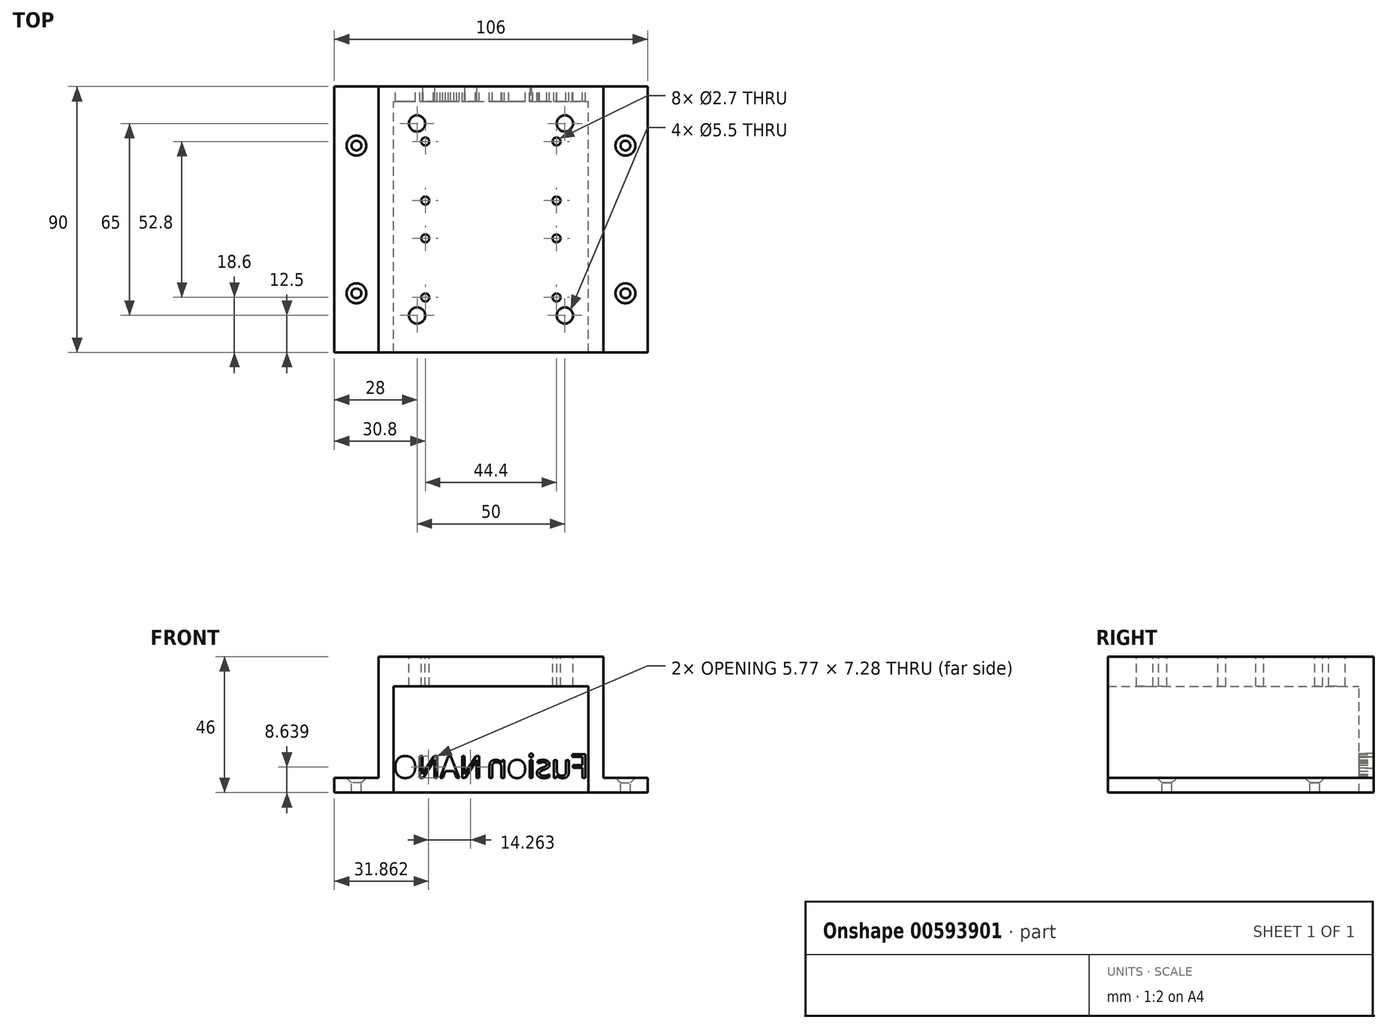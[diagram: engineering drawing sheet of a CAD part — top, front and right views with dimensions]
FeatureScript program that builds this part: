
annotation { "Feature Type Name" : "Feature", "Feature Type Description" : "" }
export const myFeature = defineFeature(function(context is Context, id is Id, definition is map)
    precondition{}
    {
        {
            var Q0;
            Q0=qCreatedBy(makeId("Front.planeOp"),FACE);
            var sketch = newSketch(context, id + "F0", { "sketchPlane" : qUnion([Q0])});
            skLineSegment(sketch, "E0", {"start": v(-53, 5) * mm, "end": v(-38, 5) * mm});
            skLineSegment(sketch, "E1", {"start": v(-38, 5) * mm, "end": v(-38, 46) * mm});
            skLineSegment(sketch, "E2", {"start": v(-38, 46) * mm, "end": v(0, 46) * mm});
            skLineSegment(sketch, "E3", {"start": v(0, 46) * mm, "end": v(0, 36) * mm});
            skLineSegment(sketch, "E4", {"start": v(0, 36) * mm, "end": v(-33, 36) * mm});
            skLineSegment(sketch, "E5", {"start": v(-33, 36) * mm, "end": v(-33, 0) * mm});
            skLineSegment(sketch, "E6", {"start": v(-33, 0) * mm, "end": v(-53, 0) * mm});
            skLineSegment(sketch, "E7", {"start": v(-53, 0) * mm, "end": v(-53, 5) * mm});
            skSolve(sketch);
        }
        {
            var Q0;
            Q0=makeQuery(id+"F0.imprint","IMPRINT",FACE,{"disambiguationData":[TD([[makeQuery(id+"F0.imprint","IMPRINT",EDGE,{"derivedFrom":sQuery(id+"F0.wireOp",EDGE,"E0")}),-1.0]])]});
            extrude(context, id + "F1", {"entities" : qUnion([Q0]), "depth" : 90 * mm, "offsetDistance" : 25 * mm});
        }
        {
            var Q0;
            Q0=makeQuery(id+"F1.opExtrude","SWEPT_FACE",FACE,{"disambiguationData":[OSD([sQuery(id+"F0.wireOp",EDGE,"E0")])]});
            var sketch = newSketch(context, id + "F2", { "sketchPlane" : qUnion([Q0])});
            skLineSegment(sketch, "E8", {"start": v(-45.5, 0) * mm, "end": v(-45.5, -90) * mm, "construction": true});
            skPoint(sketch, "E9", {"position": v(-45.5, -20) * mm});
            skPoint(sketch, "E10", {"position": v(-45.5, -70) * mm});
            skPoint(sketch, "E11", {"position": v(-45.5, -45) * mm});
            skSolve(sketch);
        }
        {
            var Q0;
            Q0=sQuery(id+"F2.wireOp",VERTEX,"E9");
            var Q1;
            Q1=sQuery(id+"F2.wireOp",VERTEX,"E10");
            var Q2;
            Q2=makeQuery(id+"F1.opExtrude","SWEPT_BODY",BODY,{"disambiguationData":[OSD([sQuery(id+"F0.wireOp",EDGE,"E0"),sQuery(id+"F0.wireOp",EDGE,"E1"),sQuery(id+"F0.wireOp",EDGE,"E2"),sQuery(id+"F0.wireOp",EDGE,"E3"),sQuery(id+"F0.wireOp",EDGE,"E4"),sQuery(id+"F0.wireOp",EDGE,"E5"),sQuery(id+"F0.wireOp",EDGE,"E6"),sQuery(id+"F0.wireOp",EDGE,"E7")])]});
            hole(context, id + "F3", {"style" : HoleStyle.C_SINK, "endStyle" : HoleEndStyle.THROUGH, "standardTappedOrClearance" : lookupTablePath({ "standard" : "ISO", "fit" : "Normal", "size" : "M3", "type" : "Clearance" }), "standardBlindInLast" : lookupTablePath({ "fit" : "Standard", "standard" : "ISO", "size" : "M3", "type" : "Clearance" }), "holeDiameter" : 3.3 * mm, "cSinkDiameter" : 6.72 * mm, "cSinkAngle" : 90 * degree, "majorDiameter" : 5 * mm, "isTappedThrough" : true, "tappedDepth" : 12 * mm, "tapClearance" : 3, "locations" : qUnion([Q0, Q1]), "scope" : qUnion([Q2])});
        }
        {
            var Q0;
            Q0=makeQuery(id+"F1.opExtrude","SWEPT_BODY",BODY,{"disambiguationData":[OSD([sQuery(id+"F0.wireOp",EDGE,"E0"),sQuery(id+"F0.wireOp",EDGE,"E1"),sQuery(id+"F0.wireOp",EDGE,"E2"),sQuery(id+"F0.wireOp",EDGE,"E3"),sQuery(id+"F0.wireOp",EDGE,"E4"),sQuery(id+"F0.wireOp",EDGE,"E5"),sQuery(id+"F0.wireOp",EDGE,"E6"),sQuery(id+"F0.wireOp",EDGE,"E7")])]});
            var Q1;
            Q1=qCreatedBy(makeId("Right.planeOp"),FACE);
            mirror(context, id + "F4", {"operationType" : NewBodyOperationType.ADD, "entities" : qUnion([Q0]), "mirrorPlane" : qUnion([Q1])});
        }
        {
            var Q0;
            {var subQ0=makeQuery(id+"F1.opExtrude","SWEPT_FACE",FACE,{"disambiguationData":[OSD([sQuery(id+"F0.wireOp",EDGE,"E4")])]});Q0=makeQuery(id+"F4.boolean.opBoolean","MERGE",FACE,{"derivedFrom":[subQ0,makeQuery(id+"F4.opPattern","COPY",FACE,{"derivedFrom":subQ0,"instanceName":"1"})]});}
            var sketch = newSketch(context, id + "F5", { "sketchPlane" : qUnion([Q0])});
            skLineSegment(sketch, "E12.bottom", {"start": v(-33, 0) * mm, "end": v(33, 0) * mm});
            skLineSegment(sketch, "E12.top", {"start": v(-33, 5) * mm, "end": v(33, 5) * mm});
            skLineSegment(sketch, "E12.left", {"start": v(-33, 0) * mm, "end": v(-33, 5) * mm});
            skLineSegment(sketch, "E12.right", {"start": v(33, 0) * mm, "end": v(33, 5) * mm});
            skSolve(sketch);
        }
        {
            var Q0;
            Q0=qSketchRegion(id+"F5",true);
            var Q1;
            Q1=makeQuery(id+"F4.opPattern","COPY",VERTEX,{"derivedFrom":makeQuery(id+"F1.opExtrude","CAP_VERTEX",VERTEX,{"disambiguationData":[OSD([sQuery(id+"F0.wireOp",EDGE,"E5"),sQuery(id+"F0.wireOp",EDGE,"E6")])],"isStart":true}),"instanceName":"1"});
            extrude(context, id + "F6", {"entities" : qUnion([Q0]), "operationType" : NewBodyOperationType.ADD, "endBound" : BoundingType.UP_TO_VERTEX, "depth" : 25 * mm, "endBoundEntityVertex" : qUnion([Q1]), "offsetDistance" : 25 * mm});
        }
        {
            var Q0;
            Q0=makeQuery(id+"F1.opExtrude","SWEPT_EDGE",EDGE,{"disambiguationData":[OSD([sQuery(id+"F0.wireOp",EDGE,"E1"),sQuery(id+"F0.wireOp",EDGE,"E2")])]});
            cPoint(context, id + "F7", {"entities" : qUnion([Q0]), "parameter" : 0.5});
        }
        {
            var Q0;
            Q0=makeQuery(id+"F4.opPattern","COPY",EDGE,{"derivedFrom":makeQuery(id+"F1.opExtrude","SWEPT_EDGE",EDGE,{"disambiguationData":[OSD([sQuery(id+"F0.wireOp",EDGE,"E1"),sQuery(id+"F0.wireOp",EDGE,"E2")])]}),"instanceName":"1"});
            cPoint(context, id + "F8", {"entities" : qUnion([Q0]), "parameter" : 0.5});
        }
        {
            var Q0;
            Q0=makeQuery(id+"F4.opPattern","COPY",EDGE,{"derivedFrom":makeQuery(id+"F1.opExtrude","SWEPT_EDGE",EDGE,{"disambiguationData":[OSD([sQuery(id+"F0.wireOp",EDGE,"E0"),sQuery(id+"F0.wireOp",EDGE,"E7")])]}),"instanceName":"1"});
            cPoint(context, id + "F9", {"entities" : qUnion([Q0]), "parameter" : 0.5});
        }
        {
            var Q0;
            Q0 = qCreatedBy(id + "F7" ,VERTEX);
            var Q1;
            Q1 = qCreatedBy(id + "F8" ,VERTEX);
            var Q2;
            Q2 = qCreatedBy(id + "F9" ,VERTEX);
            cPlane(context, id + "F10", {"entities" : qUnion([Q0, Q1, Q2]), "cplaneType" : CPlaneType.THREE_POINT, "offset" : 25 * mm, "width" : 150 * mm, "height" : 150 * mm});
        }
        {
            var Q0;
            {var subQ0=makeQuery(id+"F1.opExtrude","SWEPT_FACE",FACE,{"disambiguationData":[OSD([sQuery(id+"F0.wireOp",EDGE,"E2")])]});Q0=makeQuery(id+"F4.boolean.opBoolean","MERGE",FACE,{"derivedFrom":[subQ0,makeQuery(id+"F4.opPattern","COPY",FACE,{"derivedFrom":subQ0,"instanceName":"1"})]});}
            var sketch = newSketch(context, id + "F11", { "sketchPlane" : qUnion([Q0])});
            skPoint(sketch, "E13", {"position": v(-25, -52.5) * mm});
            skPoint(sketch, "E14.0.1.0", {"position": v(-25, -77.5) * mm});
            skLineSegment(sketch, "E14.direction1", {"start": v(-25, -52.5) * mm, "end": v(25, -52.5) * mm, "construction": true});
            skLineSegment(sketch, "E14.direction2", {"start": v(-25, -52.5) * mm, "end": v(-25, -77.5) * mm, "construction": true});
            skPoint(sketch, "E15.0.1.0", {"position": v(25, -52.5) * mm});
            skPoint(sketch, "E15.0.1.1", {"position": v(25, -77.5) * mm});
            skPoint(sketch, "E16", {"position": v(0, -52.5) * mm});
            skPoint(sketch, "E17.MirrorP", {"position": v(25, -37.5) * mm});
            skPoint(sketch, "E18.MirrorP", {"position": v(25, -12.5) * mm});
            skPoint(sketch, "E19.MirrorP", {"position": v(0, -37.5) * mm});
            skPoint(sketch, "E20.MirrorP", {"position": v(-25, -37.5) * mm});
            skPoint(sketch, "E21.MirrorP", {"position": v(-25, -12.5) * mm});
            skLineSegment(sketch, "E22.MirrorCS", {"start": v(-25, -37.5) * mm, "end": v(-25, -12.5) * mm, "construction": true});
            skLineSegment(sketch, "E23.MirrorCS", {"start": v(-25, -37.5) * mm, "end": v(25, -37.5) * mm, "construction": true});
            skSolve(sketch);
        }
        {
            var Q0;
            Q0=sQuery(id+"F11.wireOp",VERTEX,"E21.MirrorP");
            var Q1;
            Q1=sQuery(id+"F11.wireOp",VERTEX,"E18.MirrorP");
            var Q2;
            Q2=sQuery(id+"F11.wireOp",VERTEX,"E15.0.1.1");
            var Q3;
            Q3=sQuery(id+"F11.wireOp",VERTEX,"E14.0.1.0");
            var Q4;
            Q4=makeQuery(id+"F1.opExtrude","SWEPT_BODY",BODY,{"disambiguationData":[OSD([sQuery(id+"F0.wireOp",EDGE,"E0"),sQuery(id+"F0.wireOp",EDGE,"E1"),sQuery(id+"F0.wireOp",EDGE,"E2"),sQuery(id+"F0.wireOp",EDGE,"E3"),sQuery(id+"F0.wireOp",EDGE,"E4"),sQuery(id+"F0.wireOp",EDGE,"E5"),sQuery(id+"F0.wireOp",EDGE,"E6"),sQuery(id+"F0.wireOp",EDGE,"E7")])]});
            hole(context, id + "F12", {"style" : HoleStyle.SIMPLE, "endStyle" : HoleEndStyle.THROUGH, "standardTappedOrClearance" : lookupTablePath({ "standard" : "ISO", "engagement" : "50%", "pitch" : "0.75 mm", "size" : "M6", "type" : "Tapped" }), "standardBlindInLast" : lookupTablePath({ "standard" : "ISO", "engagement" : "50%", "pitch" : "0.75 mm", "size" : "M6", "type" : "Tapped" }), "holeDiameter" : 5.5 * mm, "majorDiameter" : 6 * mm, "showTappedDepth" : true, "isTappedThrough" : true, "tappedDepth" : 12 * mm, "tapClearance" : 3, "locations" : qUnion([Q0, Q1, Q2, Q3]), "scope" : qUnion([Q4])});
        }
        {
            var Q0;
            {var subQ0=makeQuery(id+"F1.opExtrude","CAP_FACE",FACE,{"disambiguationData":[OSD([sQuery(id+"F0.wireOp",EDGE,"E0"),sQuery(id+"F0.wireOp",EDGE,"E1"),sQuery(id+"F0.wireOp",EDGE,"E2"),sQuery(id+"F0.wireOp",EDGE,"E3"),sQuery(id+"F0.wireOp",EDGE,"E4"),sQuery(id+"F0.wireOp",EDGE,"E5"),sQuery(id+"F0.wireOp",EDGE,"E6"),sQuery(id+"F0.wireOp",EDGE,"E7")])],"isStart":true});Q0=makeQuery(id+"F6.boolean.opBoolean","MERGE",FACE,{"derivedFrom":[makeQuery(id+"F4.boolean.opBoolean","MERGE",FACE,{"derivedFrom":[subQ0,makeQuery(id+"F4.opPattern","COPY",FACE,{"derivedFrom":subQ0,"instanceName":"1"})]}),makeQuery(id+"F6.opExtrude","SWEPT_FACE",FACE,{"disambiguationData":[OSD([sQuery(id+"F5.wireOp",EDGE,"E12.bottom")])]})]});}
            var sketch = newSketch(context, id + "F13", { "sketchPlane" : qUnion([Q0])});
            skText(sketch, "E24", { "text": "NANO", "fontName": "NotoSans-Regular.ttf"});
            skText(sketch, "E25", { "text": "Fusion", "fontName": "NotoSans-Regular.ttf"});
            const initialGuessF13  = {"E24": [0.003, 0.005, 1, 0, 0.00734], "E25": [-0.033, 0.005, 1, 0, 0.008]};
            skSetInitialGuess(sketch, initialGuessF13);
            skSolve(sketch);
        }
        {
            var Q0;
            Q0=qSketchRegion(id+"F13",true);
            extrude(context, id + "F14", {"entities" : qUnion([Q0]), "operationType" : NewBodyOperationType.REMOVE, "oppositeDirection" : true, "depth" : 25 * mm, "offsetDistance" : 25 * mm});
        }
        {
            var Q0;
            {var subQ0=makeQuery(id+"F1.opExtrude","CAP_FACE",FACE,{"disambiguationData":[OSD([sQuery(id+"F0.wireOp",EDGE,"E0"),sQuery(id+"F0.wireOp",EDGE,"E1"),sQuery(id+"F0.wireOp",EDGE,"E2"),sQuery(id+"F0.wireOp",EDGE,"E3"),sQuery(id+"F0.wireOp",EDGE,"E4"),sQuery(id+"F0.wireOp",EDGE,"E5"),sQuery(id+"F0.wireOp",EDGE,"E6"),sQuery(id+"F0.wireOp",EDGE,"E7")])],"isStart":true});Q0=makeQuery(id+"F14.boolean.opBoolean","SPLIT",FACE,{"disambiguationData":[TD([makeQuery(id+"F14.opExtrude","SWEPT_FACE",FACE,{"disambiguationData":[OSD([sQuery(id+"F13.wireOp",EDGE,"E25.sketch_text.stroke-72")])]})])],"derivedFrom":makeQuery(id+"F6.boolean.opBoolean","MERGE",FACE,{"derivedFrom":[makeQuery(id+"F4.boolean.opBoolean","MERGE",FACE,{"derivedFrom":[subQ0,makeQuery(id+"F4.opPattern","COPY",FACE,{"derivedFrom":subQ0,"instanceName":"1"})]}),makeQuery(id+"F6.opExtrude","SWEPT_FACE",FACE,{"disambiguationData":[OSD([sQuery(id+"F5.wireOp",EDGE,"E12.bottom")])]})]})});}
            extrude(context, id + "F15", {"entities" : qUnion([Q0]), "operationType" : NewBodyOperationType.REMOVE, "oppositeDirection" : true, "depth" : 25 * mm, "offsetDistance" : 25 * mm});
        }
        {
            var Q0;
            {var subQ0=makeQuery(id+"F1.opExtrude","CAP_FACE",FACE,{"disambiguationData":[OSD([sQuery(id+"F0.wireOp",EDGE,"E0"),sQuery(id+"F0.wireOp",EDGE,"E1"),sQuery(id+"F0.wireOp",EDGE,"E2"),sQuery(id+"F0.wireOp",EDGE,"E3"),sQuery(id+"F0.wireOp",EDGE,"E4"),sQuery(id+"F0.wireOp",EDGE,"E5"),sQuery(id+"F0.wireOp",EDGE,"E6"),sQuery(id+"F0.wireOp",EDGE,"E7")])],"isStart":true});Q0=makeQuery(id+"F14.boolean.opBoolean","SPLIT",FACE,{"disambiguationData":[TD([makeQuery(id+"F14.opExtrude","SWEPT_FACE",FACE,{"disambiguationData":[OSD([sQuery(id+"F13.wireOp",EDGE,"E24.sketch_text.stroke-57")])]})])],"derivedFrom":makeQuery(id+"F6.boolean.opBoolean","MERGE",FACE,{"derivedFrom":[makeQuery(id+"F4.boolean.opBoolean","MERGE",FACE,{"derivedFrom":[subQ0,makeQuery(id+"F4.opPattern","COPY",FACE,{"derivedFrom":subQ0,"instanceName":"1"})]}),makeQuery(id+"F6.opExtrude","SWEPT_FACE",FACE,{"disambiguationData":[OSD([sQuery(id+"F5.wireOp",EDGE,"E12.bottom")])]})]})});}
            extrude(context, id + "F16", {"entities" : qUnion([Q0]), "operationType" : NewBodyOperationType.REMOVE, "oppositeDirection" : true, "depth" : 25 * mm, "offsetDistance" : 25 * mm});
        }
        {
            var Q0;
            {var subQ0=makeQuery(id+"F1.opExtrude","CAP_FACE",FACE,{"disambiguationData":[OSD([sQuery(id+"F0.wireOp",EDGE,"E0"),sQuery(id+"F0.wireOp",EDGE,"E1"),sQuery(id+"F0.wireOp",EDGE,"E2"),sQuery(id+"F0.wireOp",EDGE,"E3"),sQuery(id+"F0.wireOp",EDGE,"E4"),sQuery(id+"F0.wireOp",EDGE,"E5"),sQuery(id+"F0.wireOp",EDGE,"E6"),sQuery(id+"F0.wireOp",EDGE,"E7")])],"isStart":true});Q0=makeQuery(id+"F14.boolean.opBoolean","SPLIT",FACE,{"disambiguationData":[TD([makeQuery(id+"F14.opExtrude","SWEPT_FACE",FACE,{"disambiguationData":[OSD([sQuery(id+"F13.wireOp",EDGE,"E24.sketch_text.stroke-26")])]})])],"derivedFrom":makeQuery(id+"F6.boolean.opBoolean","MERGE",FACE,{"derivedFrom":[makeQuery(id+"F4.boolean.opBoolean","MERGE",FACE,{"derivedFrom":[subQ0,makeQuery(id+"F4.opPattern","COPY",FACE,{"derivedFrom":subQ0,"instanceName":"1"})]}),makeQuery(id+"F6.opExtrude","SWEPT_FACE",FACE,{"disambiguationData":[OSD([sQuery(id+"F5.wireOp",EDGE,"E12.bottom")])]})]})});}
            extrude(context, id + "F17", {"entities" : qUnion([Q0]), "operationType" : NewBodyOperationType.REMOVE, "oppositeDirection" : true, "depth" : 25 * mm, "offsetDistance" : 25 * mm});
        }
        {
            var Q0;
            {var subQ0=makeQuery(id+"F1.opExtrude","SWEPT_FACE",FACE,{"disambiguationData":[OSD([sQuery(id+"F0.wireOp",EDGE,"E2")])]});Q0=makeQuery(id+"F4.boolean.opBoolean","MERGE",FACE,{"derivedFrom":[subQ0,makeQuery(id+"F4.opPattern","COPY",FACE,{"derivedFrom":subQ0,"instanceName":"1"})]});}
            var sketch = newSketch(context, id + "F18", { "sketchPlane" : qUnion([Q0])});
            skPoint(sketch, "E26", {"position": v(-22.2, -18.6) * mm});
            skPoint(sketch, "E27.0.1.0", {"position": v(-22.2, -38.6) * mm});
            skPoint(sketch, "E27.1.0.0", {"position": v(22.2, -18.6) * mm});
            skPoint(sketch, "E27.1.1.0", {"position": v(22.2, -38.6) * mm});
            skLineSegment(sketch, "E27.direction1", {"start": v(-22.2, -18.6) * mm, "end": v(22.2, -18.6) * mm, "construction": true});
            skLineSegment(sketch, "E27.direction2", {"start": v(-22.2, -18.6) * mm, "end": v(-22.2, -38.6) * mm, "construction": true});
            skLineSegment(sketch, "E28.MirrorCS", {"start": v(-22.2, -71.4) * mm, "end": v(-22.2, -51.4) * mm, "construction": true});
            skLineSegment(sketch, "E29.MirrorCS", {"start": v(-22.2, -71.4) * mm, "end": v(22.2, -71.4) * mm, "construction": true});
            skPoint(sketch, "E30.MirrorP", {"position": v(-22.2, -71.4) * mm});
            skPoint(sketch, "E31.MirrorP", {"position": v(22.2, -71.4) * mm});
            skPoint(sketch, "E32.MirrorP", {"position": v(-22.2, -51.4) * mm});
            skPoint(sketch, "E33.MirrorP", {"position": v(22.2, -51.4) * mm});
            skSolve(sketch);
        }
        {
            var Q0;
            Q0=sQuery(id+"F18.wireOp",VERTEX,"E27.1.0.0");
            var Q1;
            Q1=sQuery(id+"F18.wireOp",VERTEX,"E27.1.1.0");
            var Q2;
            Q2=sQuery(id+"F18.wireOp",VERTEX,"E27.0.1.0");
            var Q3;
            Q3=sQuery(id+"F18.wireOp",VERTEX,"E26");
            var Q4;
            Q4=sQuery(id+"F18.wireOp",VERTEX,"E32.MirrorP");
            var Q5;
            Q5=sQuery(id+"F18.wireOp",VERTEX,"E33.MirrorP");
            var Q6;
            Q6=sQuery(id+"F18.wireOp",VERTEX,"E31.MirrorP");
            var Q7;
            Q7=sQuery(id+"F18.wireOp",VERTEX,"E30.MirrorP");
            var Q8;
            Q8=makeQuery(id+"F14.boolean.opBoolean","SPLIT",BODY,{"disambiguationData":[OD(0.0)],"derivedFrom":makeQuery(id+"F1.opExtrude","SWEPT_BODY",BODY,{"disambiguationData":[OSD([sQuery(id+"F0.wireOp",EDGE,"E0"),sQuery(id+"F0.wireOp",EDGE,"E1"),sQuery(id+"F0.wireOp",EDGE,"E2"),sQuery(id+"F0.wireOp",EDGE,"E3"),sQuery(id+"F0.wireOp",EDGE,"E4"),sQuery(id+"F0.wireOp",EDGE,"E5"),sQuery(id+"F0.wireOp",EDGE,"E6"),sQuery(id+"F0.wireOp",EDGE,"E7")])]})});
            hole(context, id + "F19", {"style" : HoleStyle.SIMPLE, "endStyle" : HoleEndStyle.THROUGH, "standardTappedOrClearance" : lookupTablePath({ "standard" : "ISO", "engagement" : "50%", "pitch" : "0.5 mm", "size" : "M3", "type" : "Tapped" }), "standardBlindInLast" : lookupTablePath({ "standard" : "ISO", "engagement" : "50%", "pitch" : "0.5 mm", "size" : "M3", "type" : "Tapped" }), "holeDiameter" : 2.7 * mm, "majorDiameter" : 3 * mm, "showTappedDepth" : true, "isTappedThrough" : true, "tappedDepth" : 12 * mm, "tapClearance" : 3, "locations" : qUnion([Q0, Q1, Q2, Q3, Q4, Q5, Q6, Q7]), "scope" : qUnion([Q8])});
        }
    });
